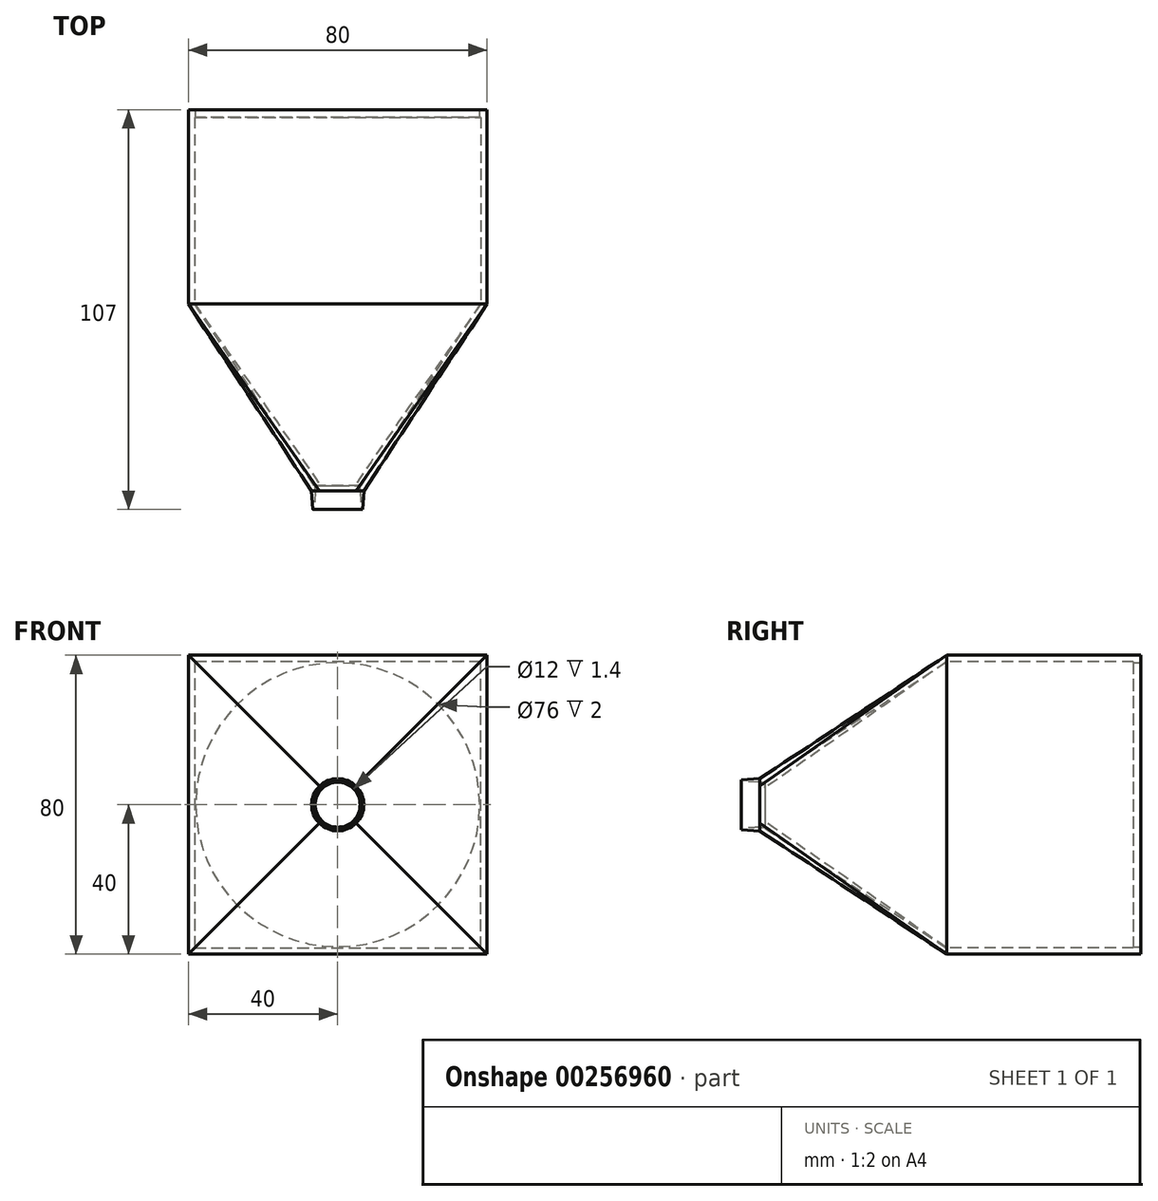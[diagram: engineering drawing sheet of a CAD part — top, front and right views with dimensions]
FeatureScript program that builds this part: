
annotation { "Feature Type Name" : "Feature", "Feature Type Description" : "" }
export const myFeature = defineFeature(function(context is Context, id is Id, definition is map)
    precondition{}
    {
        {
            var Q0;
            Q0=qCreatedBy(makeId("Front.planeOp"),FACE);
            var sketch = newSketch(context, id + "F0", { "sketchPlane" : qUnion([Q0])});
            skLineSegment(sketch, "E0.bottom", {"start": v(40, -40) * mm, "end": v(-40, -40) * mm});
            skLineSegment(sketch, "E0.top", {"start": v(40, 40) * mm, "end": v(-40, 40) * mm});
            skLineSegment(sketch, "E0.left", {"start": v(40, -40) * mm, "end": v(40, 40) * mm});
            skLineSegment(sketch, "E0.right", {"start": v(-40, -40) * mm, "end": v(-40, 40) * mm});
            skPoint(sketch, "E0.middle", {"position": v(0, 0) * mm});
            skSolve(sketch);
        }
        {
            var Q0;
            Q0=qCreatedBy(makeId("Front.planeOp"),FACE);
            cPlane(context, id + "F1", {"entities" : qUnion([Q0]), "cplaneType" : CPlaneType.OFFSET, "offset" : 50 * mm, "width" : 150 * mm, "height" : 150 * mm});
        }
        {
            var Q0;
            Q0=qCreatedBy(id+"F1.planeOp",FACE);
            var sketch = newSketch(context, id + "F2", { "sketchPlane" : qUnion([Q0])});
            skCircle(sketch, "E1", {"center": v(0, 0) * mm, "radius": 7 * mm});
            skSolve(sketch);
        }
        {
            var Q0;
            Q0=makeQuery(id+"F0.imprint","IMPRINT",FACE,{"disambiguationData":[TD([[makeQuery(id+"F0.imprint","IMPRINT",EDGE,{"derivedFrom":sQuery(id+"F0.wireOp",EDGE,"E0.bottom")}),-1.0]])]});
            var Q1;
            Q1=makeQuery(id+"F2.imprint","IMPRINT",FACE,{"disambiguationData":[TD([[makeQuery(id+"F2.imprint","IMPRINT",EDGE,{"derivedFrom":sQuery(id+"F2.wireOp",EDGE,"E1")}),1.0]])]});
            loft(context, id + "F3", {"sheetProfilesArray" : [{ "sheetProfileEntities" : qUnion([Q0]) }, { "sheetProfileEntities" : qUnion([Q1]) }]});
        }
        {
            var Q0;
            Q0=makeQuery(id+"F3.opLoft","CAP_FACE",FACE,{"disambiguationData":[OSD([makeQuery(id+"F0.imprint","IMPRINT",FACE,{"disambiguationData":[TD([[makeQuery(id+"F0.imprint","IMPRINT",EDGE,{"derivedFrom":sQuery(id+"F0.wireOp",EDGE,"E0.bottom")}),-1.0]])]})])],"isStart":true});
            shell(context, id + "F4", {"entities" : qUnion([Q0]), "thickness" : 1.4 * mm});
        }
        {
            var Q0;
            Q0=makeQuery(id+"F4.opShell","OFFSET_FACE",FACE,{"disambiguationData":[OSD([makeQuery(id+"F2.imprint","IMPRINT",FACE,{"disambiguationData":[TD([[makeQuery(id+"F2.imprint","IMPRINT",EDGE,{"derivedFrom":sQuery(id+"F2.wireOp",EDGE,"E1")}),1.0]])]})])]});
            var sketch = newSketch(context, id + "F5", { "sketchPlane" : qUnion([Q0])});
            skCircle(sketch, "E2", {"center": v(0, 0) * mm, "radius": 6 * mm});
            skSolve(sketch);
        }
        {
            var Q0;
            Q0 = qSketchRegion(id + "F5", true);
            extrude(context, id + "F6", {"entities" : qUnion([Q0]), "operationType" : NewBodyOperationType.REMOVE, "oppositeDirection" : true, "depth" : 25 * mm});
        }
        {
            var Q0;
            Q0=makeQuery(id+"F3.opLoft","CAP_FACE",FACE,{"disambiguationData":[OSD([makeQuery(id+"F0.imprint","IMPRINT",FACE,{"disambiguationData":[TD([[makeQuery(id+"F0.imprint","IMPRINT",EDGE,{"derivedFrom":sQuery(id+"F0.wireOp",EDGE,"E0.bottom")}),-1.0]])]})])],"isStart":true});
            var sketch = newSketch(context, id + "F7", { "sketchPlane" : qUnion([Q0])});
            skLineSegment(sketch, "E3.bottom", {"start": v(40, -40) * mm, "end": v(-40, -40) * mm});
            skLineSegment(sketch, "E3.top", {"start": v(40, 40) * mm, "end": v(-40, 40) * mm});
            skLineSegment(sketch, "E3.left", {"start": v(40, -40) * mm, "end": v(40, 40) * mm});
            skLineSegment(sketch, "E3.right", {"start": v(-40, -40) * mm, "end": v(-40, 40) * mm});
            skPoint(sketch, "E3.middle", {"position": v(0, 0) * mm});
            skSolve(sketch);
        }
        {
            var Q0;
            Q0=makeQuery(id+"F7.imprint","IMPRINT",FACE,{"disambiguationData":[TD([[makeQuery(id+"F7.imprint","IMPRINT",EDGE,{"derivedFrom":sQuery(id+"F7.wireOp",EDGE,"E3.bottom")}),-1.0]])]});
            extrude(context, id + "F8", {"entities" : qUnion([Q0]), "operationType" : NewBodyOperationType.ADD, "depth" : 50 * mm});
        }
        {
            var Q0;
            Q0=makeQuery(id+"F8.opExtrude","CAP_FACE",FACE,{"disambiguationData":[OSD([sQuery(id+"F0.wireOp",EDGE,"E0.bottom"),sQuery(id+"F0.wireOp",EDGE,"E0.top"),sQuery(id+"F0.wireOp",EDGE,"E0.left"),sQuery(id+"F0.wireOp",EDGE,"E0.right"),sQuery(id+"F7.wireOp",EDGE,"E3.bottom"),sQuery(id+"F7.wireOp",EDGE,"E3.top"),sQuery(id+"F7.wireOp",EDGE,"E3.left"),sQuery(id+"F7.wireOp",EDGE,"E3.right")])],"isStart":false});
            var sketch = newSketch(context, id + "F9", { "sketchPlane" : qUnion([Q0])});
            skLineSegment(sketch, "E4.bottom", {"start": v(-40, 40) * mm, "end": v(40, 40) * mm});
            skLineSegment(sketch, "E4.top", {"start": v(-40, -40) * mm, "end": v(40, -40) * mm});
            skLineSegment(sketch, "E4.left", {"start": v(-40, 40) * mm, "end": v(-40, -40) * mm});
            skLineSegment(sketch, "E4.right", {"start": v(40, 40) * mm, "end": v(40, -40) * mm});
            skSolve(sketch);
        }
        {
            var Q0;
            Q0 = qSketchRegion(id + "F9", true);
            extrude(context, id + "F10", {"entities" : qUnion([Q0]), "operationType" : NewBodyOperationType.ADD, "depth" : 2 * mm});
        }
        {
            var Q0;
            Q0=makeQuery(id+"F10.opExtrude","CAP_FACE",FACE,{"disambiguationData":[OSD([sQuery(id+"F9.wireOp",EDGE,"E4.bottom"),sQuery(id+"F9.wireOp",EDGE,"E4.top"),sQuery(id+"F9.wireOp",EDGE,"E4.left"),sQuery(id+"F9.wireOp",EDGE,"E4.right")])],"isStart":false});
            var sketch = newSketch(context, id + "F11", { "sketchPlane" : qUnion([Q0])});
            skCircle(sketch, "E5", {"center": v(0, 0) * mm, "radius": 38 * mm});
            skSolve(sketch);
        }
        {
            var Q0;
            Q0=makeQuery(id+"F11.imprint","IMPRINT",FACE,{"disambiguationData":[TD([[makeQuery(id+"F11.imprint","IMPRINT",EDGE,{"derivedFrom":sQuery(id+"F11.wireOp",EDGE,"E5")}),1.0]])]});
            extrude(context, id + "F12", {"entities" : qUnion([Q0]), "operationType" : NewBodyOperationType.REMOVE, "oppositeDirection" : true, "depth" : 25 * mm});
        }
        {
            var Q0;
            Q0=makeQuery(id+"F3.opLoft","CAP_FACE",FACE,{"disambiguationData":[OSD([makeQuery(id+"F2.imprint","IMPRINT",FACE,{"disambiguationData":[TD([[makeQuery(id+"F2.imprint","IMPRINT",EDGE,{"derivedFrom":sQuery(id+"F2.wireOp",EDGE,"E1")}),1.0]])]})])],"isStart":true});
            extrude(context, id + "F13", {"entities" : qUnion([Q0]), "operationType" : NewBodyOperationType.ADD, "depth" : 5 * mm, "hasDraft" : true, "draftAngle" : 4 * degree, "draftPullDirection" : true});
        }
    });
